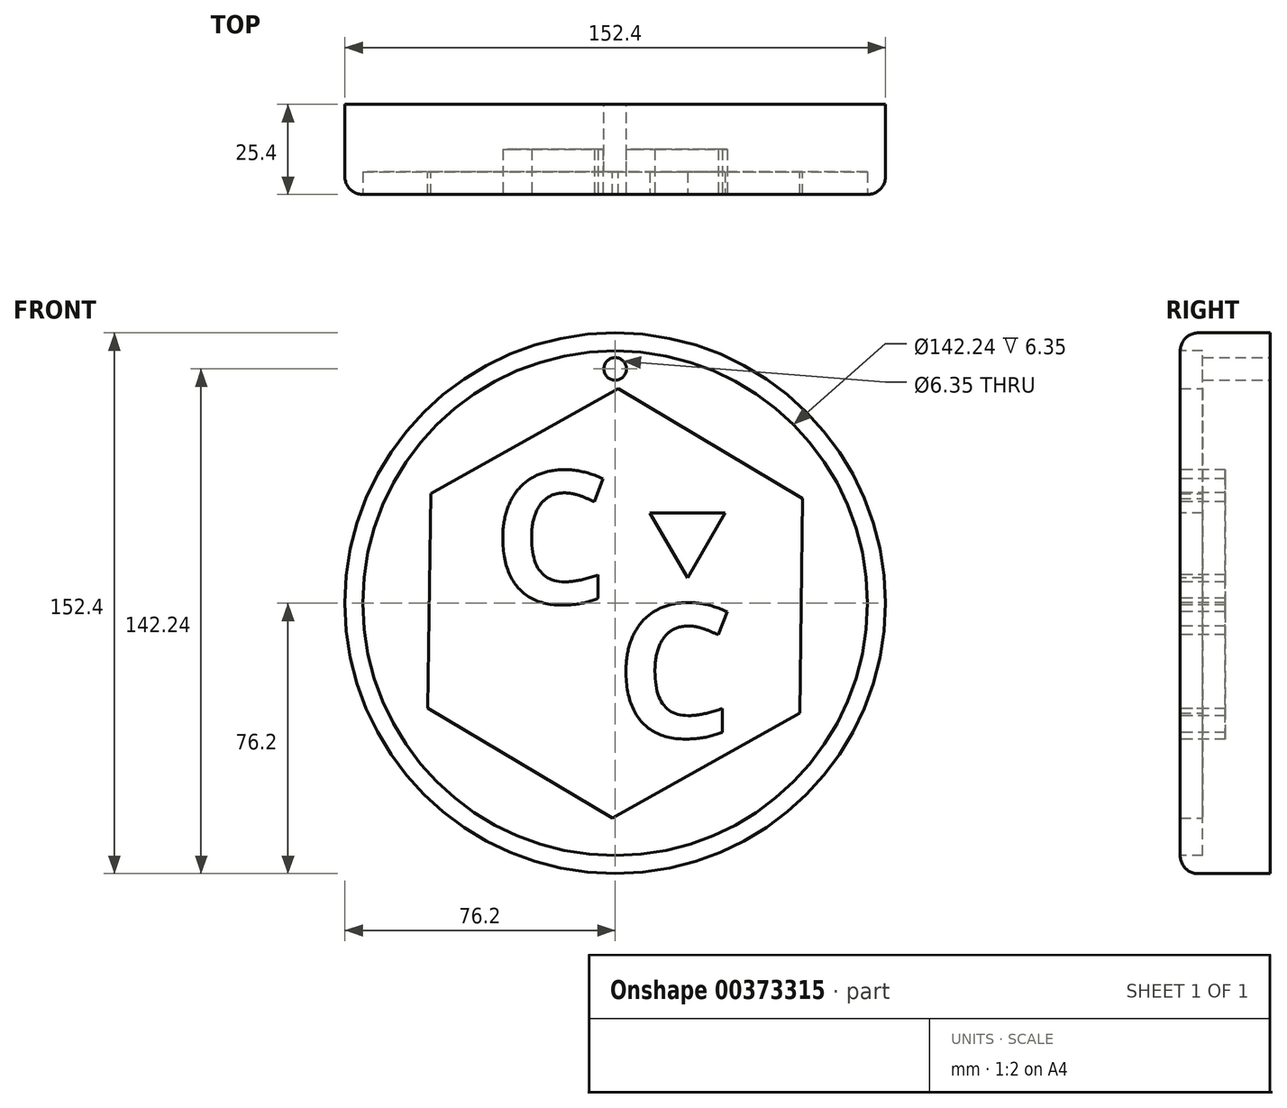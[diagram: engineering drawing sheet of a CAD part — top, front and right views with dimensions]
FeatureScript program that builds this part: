
annotation { "Feature Type Name" : "Feature", "Feature Type Description" : "" }
export const myFeature = defineFeature(function(context is Context, id is Id, definition is map)
    precondition{}
    {
        {
            var Q0;
            Q0=qCreatedBy(makeId("Front.planeOp"),FACE);
            var sketch = newSketch(context, id + "F0", { "sketchPlane" : qUnion([Q0])});
            skCircle(sketch, "E0", {"center": v(0, 0) * mm, "radius": 76.2 * mm});
            skSolve(sketch);
        }
        {
            var Q0;
            Q0=makeQuery(id+"F0.imprint","IMPRINT",FACE,{"disambiguationData":[TD([[makeQuery(id+"F0.imprint","IMPRINT",EDGE,{"derivedFrom":sQuery(id+"F0.wireOp",EDGE,"E0")}),1.0]])]});
            extrude(context, id + "F1", {"entities" : qUnion([Q0]), "depth" : 25.4 * mm});
        }
        {
            var Q0;
            Q0=makeQuery(id+"F1.opExtrude","CAP_EDGE",EDGE,{"disambiguationData":[OSD([sQuery(id+"F0.wireOp",EDGE,"E0")])],"isStart":false});
            fillet(context, id + "F2", {"entities" : qUnion([Q0]), "radius" : 5.08 * mm, "tangentPropagation" : true, "allowEdgeOverflow" : false});
        }
        {
            var Q0;
            Q0=qCreatedBy(makeId("Front.planeOp"),FACE);
            var sketch = newSketch(context, id + "F3", { "sketchPlane" : qUnion([Q0])});
            skText(sketch, "E1", { "text": "C", "fontName": "OpenSans-Bold.ttf"});
            const initialGuessF3  = {"E1": [-0.03602, 0.00032, 1, 0, 0.03888]};
            skSetInitialGuess(sketch, initialGuessF3);
            skSolve(sketch);
        }
        {
            var Q0;
            Q0=qCreatedBy(makeId("Front.planeOp"),FACE);
            var sketch = newSketch(context, id + "F4", { "sketchPlane" : qUnion([Q0])});
            skText(sketch, "E2", { "text": "W", "fontName": "OpenSans-Bold.ttf"});
            const initialGuessF4  = {"E2": [0, -0.03004, 1, 0, 0.02814]};
            skSetInitialGuess(sketch, initialGuessF4);
            skSolve(sketch);
        }
        {
            var Q0;
            Q0=makeQuery(id+"F1.opExtrude","CAP_FACE",FACE,{"disambiguationData":[OSD([sQuery(id+"F0.wireOp",EDGE,"E0")])],"isStart":false});
            extrude(context, id + "F5", {"entities" : qUnion([Q0]), "operationType" : NewBodyOperationType.REMOVE, "oppositeDirection" : true, "depth" : 6.35 * mm});
        }
        {
            var Q0;
            Q0 = qSketchRegion(id + "F3", true);
            extrude(context, id + "F6", {"entities" : qUnion([Q0]), "operationType" : NewBodyOperationType.ADD, "depth" : 25.4 * mm});
        }
        {
            var Q0;
            Q0 = qSketchRegion(id + "F4", true);
            extrude(context, id + "F7", {"entities" : qUnion([Q0]), "operationType" : NewBodyOperationType.ADD, "depth" : 25.4 * mm});
        }
        {
            var Q0;
            Q0=qCreatedBy(makeId("Front.planeOp"),FACE);
            var sketch = newSketch(context, id + "F8", { "sketchPlane" : qUnion([Q0])});
            skCircle(sketch, "E3", {"center": v(0, 66.04) * mm, "radius": 3.18 * mm});
            skSolve(sketch);
        }
        {
            var Q0;
            Q0=sQuery(id+"F8.wireOp",VERTEX,"E3.center");
            var Q1;
            Q1=makeQuery(id+"F1.opExtrude","SWEPT_BODY",BODY,{"disambiguationData":[OSD([sQuery(id+"F0.wireOp",EDGE,"E0")])]});
            hole(context, id + "F9", {"style" : HoleStyle.SIMPLE, "endStyle" : HoleEndStyle.THROUGH, "oppositeDirection" : true, "holeDiameter" : 6.35 * mm, "isTappedThrough" : true, "tappedDepth" : 12.7 * mm, "tapClearance" : 3, "locations" : qUnion([Q0]), "scope" : qUnion([Q1])});
        }
        {
            var Q0;
            Q0=qCreatedBy(makeId("Front.planeOp"),FACE);
            var sketch = newSketch(context, id + "F10", { "sketchPlane" : qUnion([Q0])});
            skCircle(sketch, "E4.cCircle", {"center": v(0, 0) * mm, "radius": 59.6 * mm, "construction": true});
            skLineSegment(sketch, "E4.0", {"start": v(-22.08, 65.17) * mm, "end": v(45.4, 51.7) * mm});
            skLineSegment(sketch, "E4.1", {"start": v(45.4, 51.7) * mm, "end": v(67.48, -13.46) * mm});
            skLineSegment(sketch, "E4.2", {"start": v(67.48, -13.46) * mm, "end": v(22.08, -65.17) * mm});
            skLineSegment(sketch, "E4.3", {"start": v(22.08, -65.17) * mm, "end": v(-45.4, -51.7) * mm});
            skLineSegment(sketch, "E4.4", {"start": v(-45.4, -51.7) * mm, "end": v(-67.48, 13.46) * mm});
            skLineSegment(sketch, "E4.5", {"start": v(-67.48, 13.46) * mm, "end": v(-22.08, 65.17) * mm});
            skPoint(sketch, "E4.0.midPoint", {"position": v(11.66, 58.44) * mm});
            skSolve(sketch);
        }
        {
            var Q0;
            Q0 = qConstructionFilter(qBodyType(qCreatedBy(id + "F10" ,EDGE), BodyType.WIRE), ConstructionObject.NO);
            extrude(context, id + "F11", {"bodyType" : ToolBodyType.SURFACE, "surfaceEntities" : qUnion([Q0]), "depth" : 25.4 * mm});
        }
        {
            var Q0;
            Q0=qCreatedBy(makeId("Front.planeOp"),FACE);
            var sketch = newSketch(context, id + "F12", { "sketchPlane" : qUnion([Q0])});
            skCircle(sketch, "E5.cCircle", {"center": v(26.58, 24.33) * mm, "radius": 14.77 * mm, "construction": true});
            skLineSegment(sketch, "E5.0", {"start": v(14.57, 34.46) * mm, "end": v(23.9, 39.8) * mm});
            skLineSegment(sketch, "E5.1", {"start": v(23.9, 39.8) * mm, "end": v(34.47, 37.91) * mm});
            skLineSegment(sketch, "E5.2", {"start": v(34.47, 37.91) * mm, "end": v(41.36, 29.66) * mm});
            skLineSegment(sketch, "E5.3", {"start": v(41.36, 29.66) * mm, "end": v(41.33, 18.91) * mm});
            skLineSegment(sketch, "E5.4", {"start": v(41.33, 18.91) * mm, "end": v(34.4, 10.7) * mm});
            skLineSegment(sketch, "E5.5", {"start": v(34.4, 10.7) * mm, "end": v(23.81, 8.86) * mm});
            skLineSegment(sketch, "E5.6", {"start": v(23.81, 8.86) * mm, "end": v(14.52, 14.26) * mm});
            skLineSegment(sketch, "E5.7", {"start": v(14.52, 14.26) * mm, "end": v(10.87, 24.37) * mm});
            skLineSegment(sketch, "E5.8", {"start": v(10.87, 24.37) * mm, "end": v(14.57, 34.46) * mm});
            skPoint(sketch, "E5.0.midPoint", {"position": v(19.23, 37.13) * mm});
            skSolve(sketch);
        }
        {
            var Q0;
            Q0 = qSketchRegion(id + "F12", true);
            extrude(context, id + "F13", {"entities" : qUnion([Q0]), "operationType" : NewBodyOperationType.ADD, "depth" : 25.4 * mm});
        }
        {
            var Q0;
            Q0=qCreatedBy(makeId("Front.planeOp"),FACE);
            var sketch = newSketch(context, id + "F14", { "sketchPlane" : qUnion([Q0])});
            skCircle(sketch, "E6.cCircle", {"center": v(0, 0) * mm, "radius": 48.27 * mm, "construction": true});
            skLineSegment(sketch, "E6.0", {"start": v(-48.27, -27.87) * mm, "end": v(-48.27, 27.87) * mm});
            skLineSegment(sketch, "E6.1", {"start": v(-48.27, 27.87) * mm, "end": v(0, 55.74) * mm});
            skLineSegment(sketch, "E6.2", {"start": v(0, 55.74) * mm, "end": v(48.27, 27.87) * mm});
            skLineSegment(sketch, "E6.3", {"start": v(48.27, 27.87) * mm, "end": v(48.27, -27.87) * mm});
            skLineSegment(sketch, "E6.4", {"start": v(48.27, -27.87) * mm, "end": v(0, -55.74) * mm});
            skLineSegment(sketch, "E6.5", {"start": v(0, -55.74) * mm, "end": v(-48.27, -27.87) * mm});
            skPoint(sketch, "E6.0.midPoint", {"position": v(-48.27, 0) * mm});
            skSolve(sketch);
        }
        {
            var Q0;
            Q0 = qSketchRegion(id + "F14", true);
            extrude(context, id + "F15", {"entities" : qUnion([Q0]), "operationType" : NewBodyOperationType.REMOVE, "oppositeDirection" : true, "depth" : 25.4 * mm});
        }
        {
            var Q0;
            Q0 = qSketchRegion(id + "F14", true);
            extrude(context, id + "F16", {"entities" : qUnion([Q0]), "operationType" : NewBodyOperationType.REMOVE, "oppositeDirection" : true, "depth" : 25.4 * mm});
        }
        {
            var Q0;
            Q0=qCreatedBy(makeId("Front.planeOp"),FACE);
            var sketch = newSketch(context, id + "F17", { "sketchPlane" : qUnion([Q0])});
            skCircle(sketch, "E7.cCircle", {"center": v(0, 0) * mm, "radius": 52.41 * mm, "construction": true});
            skLineSegment(sketch, "E7.0", {"start": v(0.82, 60.52) * mm, "end": v(52.82, 29.55) * mm});
            skLineSegment(sketch, "E7.1", {"start": v(52.82, 29.55) * mm, "end": v(52, -30.96) * mm});
            skLineSegment(sketch, "E7.2", {"start": v(52, -30.96) * mm, "end": v(-0.82, -60.52) * mm});
            skLineSegment(sketch, "E7.3", {"start": v(-0.82, -60.52) * mm, "end": v(-52.82, -29.55) * mm});
            skLineSegment(sketch, "E7.4", {"start": v(-52.82, -29.55) * mm, "end": v(-52, 30.96) * mm});
            skLineSegment(sketch, "E7.5", {"start": v(-52, 30.96) * mm, "end": v(0.82, 60.52) * mm});
            skPoint(sketch, "E7.0.midPoint", {"position": v(26.82, 45.03) * mm});
            skSolve(sketch);
        }
        {
            var Q0;
            Q0 = qSketchRegion(id + "F17", true);
            extrude(context, id + "F18", {"entities" : qUnion([Q0]), "operationType" : NewBodyOperationType.ADD, "depth" : 25.4 * mm});
        }
        {
            var Q0;
            Q0 = qSketchRegion(id + "F17", true);
            extrude(context, id + "F19", {"entities" : qUnion([Q0]), "operationType" : NewBodyOperationType.REMOVE, "oppositeDirection" : true, "depth" : 12.7 * mm});
        }
        {
            var Q0;
            Q0=makeQuery(id+"F18.boolean.opBoolean","MERGE",FACE,{"derivedFrom":[makeQuery(id+"F6.opExtrude","CAP_FACE",FACE,{"disambiguationData":[OSD([sQuery(id+"F3.wireOp",EDGE,"E1.sketch_text.stroke-0"),sQuery(id+"F3.wireOp",EDGE,"E1.sketch_text.stroke-1"),sQuery(id+"F3.wireOp",EDGE,"E1.sketch_text.stroke-2"),sQuery(id+"F3.wireOp",EDGE,"E1.sketch_text.stroke-3"),sQuery(id+"F3.wireOp",EDGE,"E1.sketch_text.stroke-4"),sQuery(id+"F3.wireOp",EDGE,"E1.sketch_text.stroke-5"),sQuery(id+"F3.wireOp",EDGE,"E1.sketch_text.stroke-6"),sQuery(id+"F3.wireOp",EDGE,"E1.sketch_text.stroke-7"),sQuery(id+"F3.wireOp",EDGE,"E1.sketch_text.stroke-8"),sQuery(id+"F3.wireOp",EDGE,"E1.sketch_text.stroke-9"),sQuery(id+"F3.wireOp",EDGE,"E1.sketch_text.stroke-10"),sQuery(id+"F3.wireOp",EDGE,"E1.sketch_text.stroke-11"),sQuery(id+"F3.wireOp",EDGE,"E1.sketch_text.stroke-12"),sQuery(id+"F3.wireOp",EDGE,"E1.sketch_text.stroke-13"),sQuery(id+"F3.wireOp",EDGE,"E1.sketch_text.stroke-14")])],"isStart":false}),makeQuery(id+"F7.opExtrude","CAP_FACE",FACE,{"disambiguationData":[OSD([sQuery(id+"F4.wireOp",EDGE,"E2.sketch_text.stroke-0"),sQuery(id+"F4.wireOp",EDGE,"E2.sketch_text.stroke-1"),sQuery(id+"F4.wireOp",EDGE,"E2.sketch_text.stroke-2"),sQuery(id+"F4.wireOp",EDGE,"E2.sketch_text.stroke-3"),sQuery(id+"F4.wireOp",EDGE,"E2.sketch_text.stroke-4"),sQuery(id+"F4.wireOp",EDGE,"E2.sketch_text.stroke-5"),sQuery(id+"F4.wireOp",EDGE,"E2.sketch_text.stroke-6"),sQuery(id+"F4.wireOp",EDGE,"E2.sketch_text.stroke-7"),sQuery(id+"F4.wireOp",EDGE,"E2.sketch_text.stroke-8"),sQuery(id+"F4.wireOp",EDGE,"E2.sketch_text.stroke-9"),sQuery(id+"F4.wireOp",EDGE,"E2.sketch_text.stroke-10"),sQuery(id+"F4.wireOp",EDGE,"E2.sketch_text.stroke-11"),sQuery(id+"F4.wireOp",EDGE,"E2.sketch_text.stroke-12"),sQuery(id+"F4.wireOp",EDGE,"E2.sketch_text.stroke-13"),sQuery(id+"F4.wireOp",EDGE,"E2.sketch_text.stroke-14"),sQuery(id+"F4.wireOp",EDGE,"E2.sketch_text.stroke-15"),sQuery(id+"F4.wireOp",EDGE,"E2.sketch_text.stroke-16"),sQuery(id+"F4.wireOp",EDGE,"E2.sketch_text.stroke-17"),sQuery(id+"F4.wireOp",EDGE,"E2.sketch_text.stroke-18"),sQuery(id+"F4.wireOp",EDGE,"E2.sketch_text.stroke-19"),sQuery(id+"F4.wireOp",EDGE,"E2.sketch_text.stroke-20"),sQuery(id+"F4.wireOp",EDGE,"E2.sketch_text.stroke-21"),sQuery(id+"F4.wireOp",EDGE,"E2.sketch_text.stroke-22"),sQuery(id+"F4.wireOp",EDGE,"E2.sketch_text.stroke-23")])],"isStart":false}),makeQuery(id+"F13.opExtrude","CAP_FACE",FACE,{"disambiguationData":[OSD([sQuery(id+"F12.wireOp",EDGE,"E5.0"),sQuery(id+"F12.wireOp",EDGE,"E5.1"),sQuery(id+"F12.wireOp",EDGE,"E5.2"),sQuery(id+"F12.wireOp",EDGE,"E5.3"),sQuery(id+"F12.wireOp",EDGE,"E5.4"),sQuery(id+"F12.wireOp",EDGE,"E5.5"),sQuery(id+"F12.wireOp",EDGE,"E5.6"),sQuery(id+"F12.wireOp",EDGE,"E5.7"),sQuery(id+"F12.wireOp",EDGE,"E5.8")])],"isStart":false}),makeQuery(id+"F18.opExtrude","CAP_FACE",FACE,{"disambiguationData":[OSD([sQuery(id+"F17.wireOp",EDGE,"E7.0"),sQuery(id+"F17.wireOp",EDGE,"E7.1"),sQuery(id+"F17.wireOp",EDGE,"E7.2"),sQuery(id+"F17.wireOp",EDGE,"E7.3"),sQuery(id+"F17.wireOp",EDGE,"E7.4"),sQuery(id+"F17.wireOp",EDGE,"E7.5")])],"isStart":false})]});
            var sketch = newSketch(context, id + "F20", { "sketchPlane" : qUnion([Q0])});
            skText(sketch, "E8", { "text": "C", "fontName": "OpenSans-Bold.ttf"});
            const initialGuessF20  = {"E8": [-0.0347, 0, 1, 0, 0.03745]};
            skSetInitialGuess(sketch, initialGuessF20);
            skSolve(sketch);
        }
        {
            var Q0;
            Q0=makeQuery(id+"F20.imprint","IMPRINT",FACE,{"disambiguationData":[TD([[makeQuery(id+"F20.imprint","IMPRINT",EDGE,{"derivedFrom":sQuery(id+"F20.wireOp",EDGE,"E8.sketch_text.stroke-0")}),1.0]])]});
            var sketch = newSketch(context, id + "F21", { "sketchPlane" : qUnion([Q0])});
            skText(sketch, "E9", { "text": "C", "fontName": "OpenSans-Bold.ttf"});
            const initialGuessF21  = {"E9": [0, -0.03775, 1, 0, 0.03775]};
            skSetInitialGuess(sketch, initialGuessF21);
            skSolve(sketch);
        }
        {
            var Q0;
            Q0 = qSketchRegion(id + "F20", true);
            extrude(context, id + "F22", {"entities" : qUnion([Q0]), "operationType" : NewBodyOperationType.REMOVE, "oppositeDirection" : true, "depth" : 12.7 * mm});
        }
        {
            var Q0;
            Q0 = qSketchRegion(id + "F21", true);
            extrude(context, id + "F23", {"entities" : qUnion([Q0]), "operationType" : NewBodyOperationType.REMOVE, "oppositeDirection" : true, "depth" : 12.7 * mm});
        }
        {
            var Q0;
            Q0=makeQuery(id+"F18.boolean.opBoolean","MERGE",FACE,{"derivedFrom":[makeQuery(id+"F6.opExtrude","CAP_FACE",FACE,{"disambiguationData":[OSD([sQuery(id+"F3.wireOp",EDGE,"E1.sketch_text.stroke-0"),sQuery(id+"F3.wireOp",EDGE,"E1.sketch_text.stroke-1"),sQuery(id+"F3.wireOp",EDGE,"E1.sketch_text.stroke-2"),sQuery(id+"F3.wireOp",EDGE,"E1.sketch_text.stroke-3"),sQuery(id+"F3.wireOp",EDGE,"E1.sketch_text.stroke-4"),sQuery(id+"F3.wireOp",EDGE,"E1.sketch_text.stroke-5"),sQuery(id+"F3.wireOp",EDGE,"E1.sketch_text.stroke-6"),sQuery(id+"F3.wireOp",EDGE,"E1.sketch_text.stroke-7"),sQuery(id+"F3.wireOp",EDGE,"E1.sketch_text.stroke-8"),sQuery(id+"F3.wireOp",EDGE,"E1.sketch_text.stroke-9"),sQuery(id+"F3.wireOp",EDGE,"E1.sketch_text.stroke-10"),sQuery(id+"F3.wireOp",EDGE,"E1.sketch_text.stroke-11"),sQuery(id+"F3.wireOp",EDGE,"E1.sketch_text.stroke-12"),sQuery(id+"F3.wireOp",EDGE,"E1.sketch_text.stroke-13"),sQuery(id+"F3.wireOp",EDGE,"E1.sketch_text.stroke-14")])],"isStart":false}),makeQuery(id+"F7.opExtrude","CAP_FACE",FACE,{"disambiguationData":[OSD([sQuery(id+"F4.wireOp",EDGE,"E2.sketch_text.stroke-0"),sQuery(id+"F4.wireOp",EDGE,"E2.sketch_text.stroke-1"),sQuery(id+"F4.wireOp",EDGE,"E2.sketch_text.stroke-2"),sQuery(id+"F4.wireOp",EDGE,"E2.sketch_text.stroke-3"),sQuery(id+"F4.wireOp",EDGE,"E2.sketch_text.stroke-4"),sQuery(id+"F4.wireOp",EDGE,"E2.sketch_text.stroke-5"),sQuery(id+"F4.wireOp",EDGE,"E2.sketch_text.stroke-6"),sQuery(id+"F4.wireOp",EDGE,"E2.sketch_text.stroke-7"),sQuery(id+"F4.wireOp",EDGE,"E2.sketch_text.stroke-8"),sQuery(id+"F4.wireOp",EDGE,"E2.sketch_text.stroke-9"),sQuery(id+"F4.wireOp",EDGE,"E2.sketch_text.stroke-10"),sQuery(id+"F4.wireOp",EDGE,"E2.sketch_text.stroke-11"),sQuery(id+"F4.wireOp",EDGE,"E2.sketch_text.stroke-12"),sQuery(id+"F4.wireOp",EDGE,"E2.sketch_text.stroke-13"),sQuery(id+"F4.wireOp",EDGE,"E2.sketch_text.stroke-14"),sQuery(id+"F4.wireOp",EDGE,"E2.sketch_text.stroke-15"),sQuery(id+"F4.wireOp",EDGE,"E2.sketch_text.stroke-16"),sQuery(id+"F4.wireOp",EDGE,"E2.sketch_text.stroke-17"),sQuery(id+"F4.wireOp",EDGE,"E2.sketch_text.stroke-18"),sQuery(id+"F4.wireOp",EDGE,"E2.sketch_text.stroke-19"),sQuery(id+"F4.wireOp",EDGE,"E2.sketch_text.stroke-20"),sQuery(id+"F4.wireOp",EDGE,"E2.sketch_text.stroke-21"),sQuery(id+"F4.wireOp",EDGE,"E2.sketch_text.stroke-22"),sQuery(id+"F4.wireOp",EDGE,"E2.sketch_text.stroke-23")])],"isStart":false}),makeQuery(id+"F13.opExtrude","CAP_FACE",FACE,{"disambiguationData":[OSD([sQuery(id+"F12.wireOp",EDGE,"E5.0"),sQuery(id+"F12.wireOp",EDGE,"E5.1"),sQuery(id+"F12.wireOp",EDGE,"E5.2"),sQuery(id+"F12.wireOp",EDGE,"E5.3"),sQuery(id+"F12.wireOp",EDGE,"E5.4"),sQuery(id+"F12.wireOp",EDGE,"E5.5"),sQuery(id+"F12.wireOp",EDGE,"E5.6"),sQuery(id+"F12.wireOp",EDGE,"E5.7"),sQuery(id+"F12.wireOp",EDGE,"E5.8")])],"isStart":false}),makeQuery(id+"F18.opExtrude","CAP_FACE",FACE,{"disambiguationData":[OSD([sQuery(id+"F17.wireOp",EDGE,"E7.0"),sQuery(id+"F17.wireOp",EDGE,"E7.1"),sQuery(id+"F17.wireOp",EDGE,"E7.2"),sQuery(id+"F17.wireOp",EDGE,"E7.3"),sQuery(id+"F17.wireOp",EDGE,"E7.4"),sQuery(id+"F17.wireOp",EDGE,"E7.5")])],"isStart":false})]});
            var sketch = newSketch(context, id + "F24", { "sketchPlane" : qUnion([Q0])});
            skCircle(sketch, "E10.cCircle", {"center": v(20.4, 19.38) * mm, "radius": 6.12 * mm, "construction": true});
            skLineSegment(sketch, "E10.0", {"start": v(9.8, 25.5) * mm, "end": v(31, 25.5) * mm});
            skLineSegment(sketch, "E10.1", {"start": v(31, 25.5) * mm, "end": v(20.4, 7.14) * mm});
            skLineSegment(sketch, "E10.2", {"start": v(20.4, 7.14) * mm, "end": v(9.8, 25.5) * mm});
            skPoint(sketch, "E10.0.midPoint", {"position": v(20.4, 25.5) * mm});
            skSolve(sketch);
        }
        {
            var Q0;
            Q0 = qSketchRegion(id + "F24", true);
            extrude(context, id + "F25", {"entities" : qUnion([Q0]), "operationType" : NewBodyOperationType.REMOVE, "oppositeDirection" : true, "depth" : 6.35 * mm});
        }
    });
